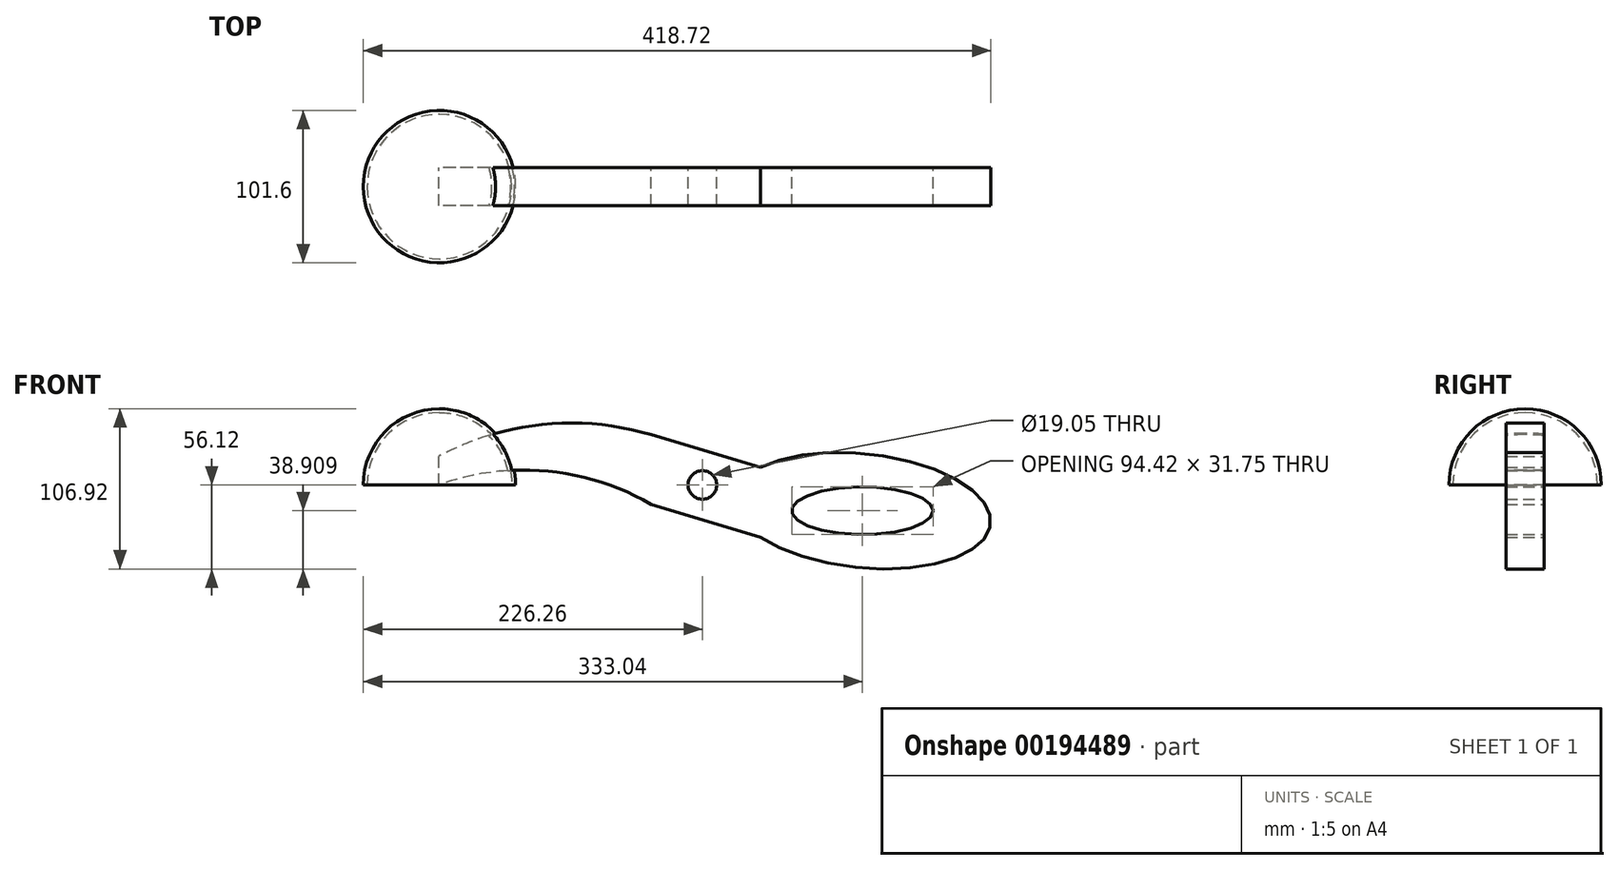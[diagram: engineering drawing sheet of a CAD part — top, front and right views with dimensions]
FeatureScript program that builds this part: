
annotation { "Feature Type Name" : "Feature", "Feature Type Description" : "" }
export const myFeature = defineFeature(function(context is Context, id is Id, definition is map)
    precondition{}
    {
        {
            var Q0;
            Q0=qCreatedBy(makeId("Front.planeOp"),FACE);
            var sketch = newSketch(context, id + "F0", { "sketchPlane" : qUnion([Q0])});
            skCircle(sketch, "E0", {"center": v(0, 0) * mm, "radius": 9.53 * mm});
            skLineSegment(sketch, "E1", {"start": v(-34.35, 33.5) * mm, "end": v(38.65, 11.62) * mm});
            skLineSegment(sketch, "E2", {"start": v(-34.35, -12.9) * mm, "end": v(38.65, -34.78) * mm});
            skArc(sketch, "E3", {"start": v(-34.35, 33.5) * mm, "mid": v(-106.57, 40.35) * mm, "end": v(-175.91, 19.05) * mm});
            skArc(sketch, "E4", {"start": v(-34.35, -12.9) * mm, "mid": v(-103.7, 9.2) * mm, "end": v(-175.91, 0) * mm});
            skLineSegment(sketch, "E5", {"start": v(-175.91, 0) * mm, "end": v(-175.91, 19.05) * mm});
            skEllipse(sketch, "E6", {"center": v(106.78, -17.21) * mm, "majorRadius": 47.21 * mm, "minorRadius": 15.88 * mm, "majorAxis": v(1, 0)});
            skEllipse(sketch, "E7", {"center": v(106.78, -17.21) * mm, "majorRadius": 86.05 * mm, "minorRadius": 38.1 * mm, "majorAxis": v(1, -0.1)});
            skSolve(sketch);
        }
        {
            var Q0;
            Q0=makeQuery(id+"F0.imprint","IMPRINT",FACE,{"disambiguationData":[TD([[makeQuery(id+"F0.imprint","IMPRINT",EDGE,{"derivedFrom":sQuery(id+"F0.wireOp",EDGE,"E0")}),-1.0]])]});
            var Q1;
            Q1=makeQuery(id+"F0.imprint","IMPRINT",FACE,{"disambiguationData":[TD([[makeQuery(id+"F0.imprint","IMPRINT",EDGE,{"derivedFrom":sQuery(id+"F0.wireOp",EDGE,"E6")}),-1.0]])]});
            extrude(context, id + "F1", {"entities" : qUnion([Q0, Q1]), "endBound" : BoundingType.SYMMETRIC, "depth" : 25.4 * mm});
        }
        {
            var Q0;
            Q0=qCreatedBy(makeId("Front.planeOp"),FACE);
            var sketch = newSketch(context, id + "F2", { "sketchPlane" : qUnion([Q0])});
            skLineSegment(sketch, "E8", {"start": v(-175.46, 0) * mm, "end": v(-175.46, 63) * mm});
            skArc(sketch, "E9", {"start": v(-175.46, 50.8) * mm, "mid": v(-139.54, 35.92) * mm, "end": v(-124.66, 0) * mm});
            skArc(sketch, "E10.0", {"start": v(-175.46, 48.26) * mm, "mid": v(-141.33, 34.12) * mm, "end": v(-127.2, 0) * mm});
            skLineSegment(sketch, "E11", {"start": v(-127.2, 0) * mm, "end": v(-124.66, 0) * mm});
            skSolve(sketch);
        }
        {
            var Q0;
            Q0 = qSketchRegion(id + "F2", true);
            var Q1;
            Q1=sQuery(id+"F2.wireOp",EDGE,"E8");
            revolve(context, id + "F3", {"operationType" : NewBodyOperationType.ADD, "entities" : qUnion([Q0]), "axis" : qUnion([Q1]), "revolveType" : RevolveType.FULL});
        }
    });
